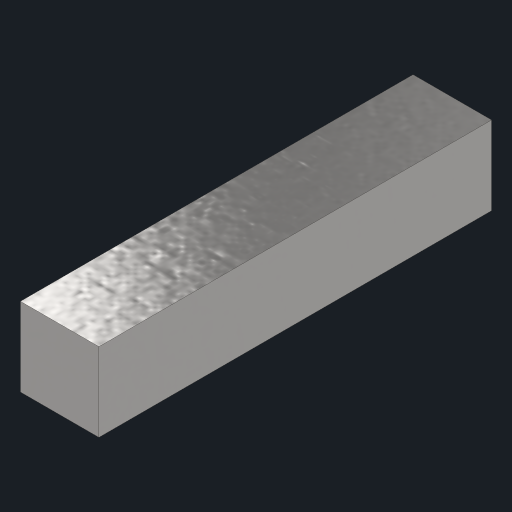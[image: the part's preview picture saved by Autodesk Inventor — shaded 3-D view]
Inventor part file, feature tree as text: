
AUTODESK INVENTOR PART (.ipt)
format: ipt  version: 2024 (Build 280153000, 153)  size: 133,632 bytes
history: native  units: in
note: dims shown in document units (in); Inventor stores cm internally (conversion verified against a paired STEP export)
features: extrude x1, sketch x1
ambient origin geometry x8: Origin, YZ Plane, XZ Plane, XY Plane, X Axis, Y Axis, Z Axis, Center Point
bodies: Solid1 (feature_tree)
feature tree (2):
  extrude  "Extrusion1"  Depth=0.3937in TaperAngle=0.0deg
  sketch  "Sketch1"  dims[d0=0.0787in d1=0.3937in d2=0.0in]
